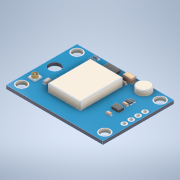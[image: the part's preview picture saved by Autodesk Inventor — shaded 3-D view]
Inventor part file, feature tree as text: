
AUTODESK INVENTOR PART (.ipt)
format: ipt  version: 2021 (Build 250183000, 183)  size: 295,936 bytes
history: mixed  units: in
note: dims shown in document units (in); Inventor stores cm internally (conversion verified against a paired STEP export)
features: fillet x1, imported_body x1
ambient origin geometry x8: Origin, YZ Plane, XZ Plane, XY Plane, X Axis, Y Axis, Z Axis, Center Point
bodies: Solid1 (imported_parasolid)
feature tree (2):
  fillet  "Congé8"  [1 undecoded]
  imported_body  NMx_Import_Brep_tag  [imported B-rep: ~183 faces, bbox_mm=[35.6, 4.06, 26.08]]
note: 1 required parameter value undecoded (feature->parameter linkage not recoverable at this tier; creation-order binding heuristic only, values carry confidence <= 0.55)
